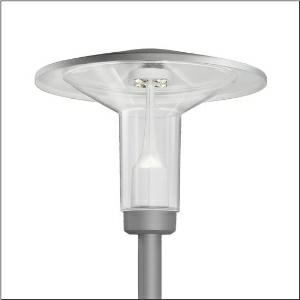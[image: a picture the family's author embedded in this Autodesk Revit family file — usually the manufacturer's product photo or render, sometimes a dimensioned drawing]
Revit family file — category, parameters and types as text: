
# Revit family: laterne_iq___st1_2a_5xa5255kf14h_a0c9
name_source: partatom
category: Lighting Fixtures
units: mm (PartAtom-declared; Revit-internal decimal feet)

## family parameters
Cut with Voids When Loaded = No
Host = Face
Light Source = No
Part Type = Normal
Room Calculation Point = No
Round Connector Dimension = Use Diameter
Shared = No

## types (1)
- --- (1 x LED, 1540 lm, 10 W, 4000K)
    Apparent Load = 10 VA
    CIE Flux Codes = 25 63 94 98 100
    Color Rendering = 70
    Color Temperature = 4000K
    Default Elevation = 1800 mm
    Description = Lantern iQ, mast luminaire, Module 540 iQ-SR, primary light control with 3 zone facetted reflector, of plastic, silver coated, highly specular, structured, primary optical cover: cover, of PMMA, transparent, light distribution: ST1.2a, light emission: direct distribution, primary light characteristic: asymmetric, installation type: post-top, LED, High Power LED, rated luminous flux: 1.540lm, luminous efficacy: 154lm/W, light colour: 740, colour temperature: 4000K, control gear: ECG iQ, control: presetting dimming logarithmic, Street-Remote, Auto-Match, Temp-Guard, Lumen-Switch, Night-Set, Smart-Wire, Light-Fading, Desk-Remote (wireless, voltage-free reading and setting of iQ features in the workshop via application-optimized NFC function/RFID function), optimised constant luminous flux control (CLO 2.0), with terminal, 6-pole, max. 2.5mm², mains connection: 220..240V, AC, 50/60Hz, start of lifetime: 10W, end of lifetime: 10W, reduction: 5W, luminaire housing, upper part, of glass-fibre reinforced polyester, coated, Siteco® metallic grey (DB 702S), diameter: 750mm, height: 583mm, spigot size: d x l = 76 x 70mm (post-top) | with reducer (optional accessory) 60 x 70mm, post-top mast mounting element, of diecast aluminium, coated, Siteco® metallic grey (DB 702S), Module 540 iQ-SR, traffic white (RAL 9016), equipment: standard, protection rating (complete): IP65, insulation class (complete): insulation class II (safety insulation), certification: CE, ENEC, VDE, packaging unit: 1 piece

Light Distribution: ST1.2a
    Height = 583 mm
    Lamp = 1 x LED
    Lamp Light Flux = 1540 lm
    Lamp Power = 10 W
    Lamp count = 1
    Length = 750 mm
    Luminous efficacy = 154 lm/W
    Manufacturer = Siteco
    ModVariant = No
    Model = 5XA5255KF14H
    Number of Poles = 1
    OnlyDefault = Yes
    Power Factor = 1
    Product Name = Laterne iQ | ST1.2a
    Product group = mast luminaire | pylon top
    ProductGroupID = 6100
    Protection Class = Protection class II
    Protection Degree = IP 65
    RLX_Detail_Level = 1
    RlxData = <blob elided: 107633 chars, md5=bbbecc69>
    Socket = socket
    Standby Power = 0 W
    System Light Flux = 1540 lm
    System Power = 10 W
    Type Comments = factory setting: luminous flux: 100 % | dim-lin: 254 | 401 mA
    Type Image = l_1006050.jpg
    URL = http://relux.com
    VarID = @adj_071849
    Voltage = 0 V
    Weight = 0.00 kg
    Width = 0 mm  [stored 0 ft]

note: [stored X ft] marks values corroborated as IEEE doubles in the binary element streams (Revit-internal decimal feet)

## geometry (parser evidence)
native form markers: Blend x4, Sweep x10
no freeform markers — native parametric forms only
